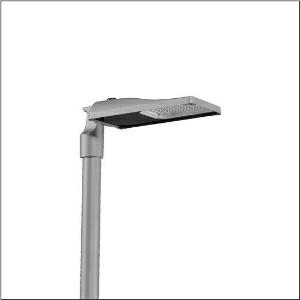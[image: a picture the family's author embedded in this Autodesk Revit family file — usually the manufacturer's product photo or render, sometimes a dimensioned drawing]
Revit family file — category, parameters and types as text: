
# Revit family: streetlight_sl_31_mini___st1_0a_5xh2d31s08ga_e80a
name_source: partatom
category: Lighting Fixtures
units: mm (PartAtom-declared; Revit-internal decimal feet)

## family parameters
Cut with Voids When Loaded = No
Host = Face
Light Source = No
Part Type = Normal
Room Calculation Point = No
Round Connector Dimension = Use Diameter
Shared = No

## types (1)
- --- (1 x LED, 5880 lm, 39.3 W, 3000K)
    Apparent Load = 39 VA
    CIE Flux Codes = 37 72 97 100 100
    Color Rendering = 70
    Color Temperature = 3000K
    Default Elevation = 1800 mm
    Description = Streetlight SL 31 mini D4i, Desk-Remote mast luminaire for post-top, side-entry; light control with lens of PMMA; light distribution: ST1.0a, direct asymmetric distribution, for standard-compliant lighting for roads and squares; LED: luminous flux: 5.880lm, light colour: 730, colour temperature: 3000K; luminous efficacy: 149,6lm/W; control: pre-setting: logarithmic dimming characteristic, flexible luminous flux parameterisation, time-dependent luminous flux control, constant luminous flux control, power reduction, intelligent temperature release in ECG and LED module, overheat protection; luminaire housing, of diecast aluminium, Siteco® metallic grey (DB 702S), corrosivity category C5 high according to DIN EN ISO 12944; cover of toughened safety glass, transparent, mast flange of diecast aluminium, Siteco® metallic grey (DB 702S), spigot size: 76/60mm, mast flange included unmounted; with cable H07RN-F 2x 1.5mm², cable length: 6,5m, connection cable pre-assembled; mains connection: 220..240V, AC, 50/60Hz; power consumption (at start of service life): 39,3W / (at end of service life): 40,7W / (with reduced operation 50%): 18,1W; protection rating (complete): IP66; insulation class (complete): insulation class II (safety insulation); impact resistance: IK10; certification: CE, ENEC, ENEC+, VDE, UKCA, ZD4i; permissible operating ambient temperature for outdoor applications: -40..+50°C; packaging unit: 1 piece

Light Distribution: ST1.0a
    Height = 76 mm
    Lamp = 1 x LED
    Lamp Light Flux = 5880 lm
    Lamp Power = 39.3 W
    Lamp count = 1
    Length = 547 mm
    Luminous efficacy = 150 lm/W
    Manufacturer = Siteco
    ModVariant = No
    Model = 5XH2D31S08GA
    Number of Poles = 1
    OnlyDefault = Yes
    Power Factor = 1
    Product Name = Streetlight SL 31 mini | ST1.0a
    Product group = mast luminaire | pylon top
    ProductGroupID = 6100
    Protection Class = Protection class II
    Protection Degree = IP 66
    RLX_Detail_Level = 1
    RLX_Emergency_Light_Flux = 0 lm
    RLX_Emergency_Type = 0
    RLX_Emergency_Type_DB = No
    RlxData = <blob elided: 39577 chars, md5=5b4ce49b>
    Socket = socket
    Standby Power = 0 W
    System Light Flux = 5880 lm
    System Power = 39 W
    Type Comments = factory setting: luminous flux: 100 % | dim-lin: 254 | 798 mA
    Type Image = l_1300330.jpg
    URL = http://relux.com
    VarID = @adj_075175
    Voltage = 0 V
    Weight = 0.00 kg
    Width = 265 mm

## geometry (parser evidence)
native form markers: Blend x4, Sweep x10
no freeform markers — native parametric forms only
